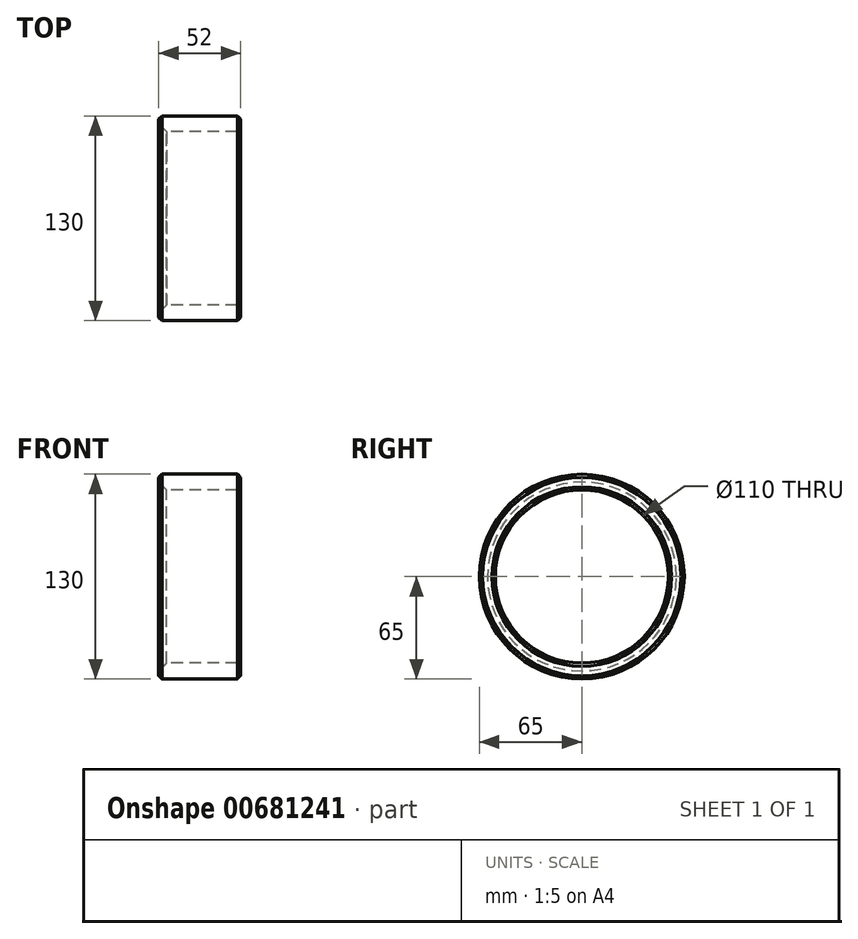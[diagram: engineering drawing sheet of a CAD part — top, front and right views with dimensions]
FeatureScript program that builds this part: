
annotation { "Feature Type Name" : "Feature", "Feature Type Description" : "" }
export const myFeature = defineFeature(function(context is Context, id is Id, definition is map)
    precondition{}
    {
        {
            var Q0;
            Q0=qCreatedBy(makeId("Right.planeOp"),FACE);
            var sketch = newSketch(context, id + "F0", { "sketchPlane" : qUnion([Q0])});
            skCircle(sketch, "E0", {"center": v(0, 0) * mm, "radius": 55 * mm});
            skCircle(sketch, "E1", {"center": v(0, 0) * mm, "radius": 65 * mm});
            skSolve(sketch);
        }
        {
            var Q0;
            Q0=makeQuery(id+"F0.imprint","IMPRINT",FACE,{"disambiguationData":[TD([[makeQuery(id+"F0.imprint","IMPRINT",EDGE,{"derivedFrom":sQuery(id+"F0.wireOp",EDGE,"E0")}),-1.0]])]});
            extrude(context, id + "F1", {"entities" : qUnion([Q0]), "endBound" : BoundingType.SYMMETRIC, "depth" : 52 * mm, "offsetDistance" : 25 * mm});
        }
        {
            var Q0;
            Q0=makeQuery(id+"F1.opExtrude","CAP_EDGE",EDGE,{"disambiguationData":[OSD([sQuery(id+"F0.wireOp",EDGE,"E0")])],"isStart":true});
            chamfer(context, id + "F2", {"entities" : qUnion([Q0]), "width" : 5 * mm, "tangentPropagation" : true});
        }
        {
            var Q0;
            Q0=makeQuery(id+"F1.opExtrude","CAP_EDGE",EDGE,{"disambiguationData":[OSD([sQuery(id+"F0.wireOp",EDGE,"E1")])],"isStart":true});
            var Q1;
            Q1=makeQuery(id+"F1.opExtrude","CAP_EDGE",EDGE,{"disambiguationData":[OSD([sQuery(id+"F0.wireOp",EDGE,"E1")])],"isStart":false});
            var Q2;
            Q2=makeQuery(id+"F1.opExtrude","CAP_EDGE",EDGE,{"disambiguationData":[OSD([sQuery(id+"F0.wireOp",EDGE,"E0")])],"isStart":false});
            chamfer(context, id + "F3", {"entities" : qUnion([Q0, Q1, Q2]), "width" : 2 * mm, "tangentPropagation" : true});
        }
    });
